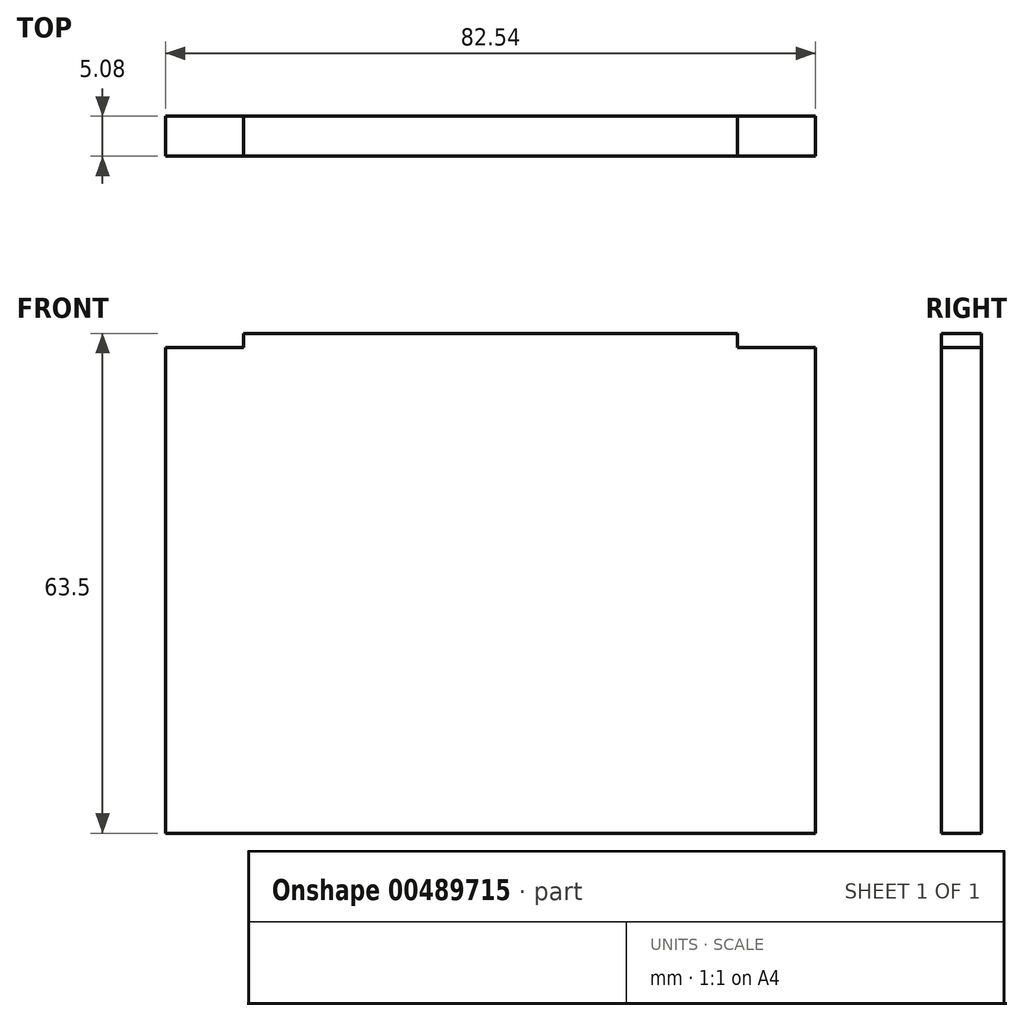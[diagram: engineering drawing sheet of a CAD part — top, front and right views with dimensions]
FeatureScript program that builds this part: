
annotation { "Feature Type Name" : "Feature", "Feature Type Description" : "" }
export const myFeature = defineFeature(function(context is Context, id is Id, definition is map)
    precondition{}
    {
        {
            var Q0;
            Q0=qCreatedBy(makeId("Front.planeOp"),FACE);
            var sketch = newSketch(context, id + "F0", { "sketchPlane" : qUnion([Q0])});
            skLineSegment(sketch, "E0.bottom", {"start": v(41.28, -31.75) * mm, "end": v(-41.28, -31.75) * mm});
            skLineSegment(sketch, "E0.top", {"start": v(31.37, 31.75) * mm, "end": v(-31.37, 31.75) * mm});
            skLineSegment(sketch, "E0.left", {"start": v(41.28, -31.75) * mm, "end": v(41.28, 29.97) * mm});
            skLineSegment(sketch, "E0.right", {"start": v(-41.28, -31.75) * mm, "end": v(-41.28, 29.97) * mm});
            skPoint(sketch, "E0.middle", {"position": v(0, 0) * mm});
            skLineSegment(sketch, "E1.top", {"start": v(-41.27, 29.97) * mm, "end": v(-31.37, 29.97) * mm});
            skLineSegment(sketch, "E1.right", {"start": v(-31.37, 31.75) * mm, "end": v(-31.37, 29.97) * mm});
            skLineSegment(sketch, "E2.MirrorCS", {"start": v(41.27, 29.97) * mm, "end": v(31.37, 29.97) * mm});
            skLineSegment(sketch, "E3.MirrorCS", {"start": v(31.37, 31.75) * mm, "end": v(31.37, 29.97) * mm});
            skPoint(sketch, "E4.orphan", {"position": v(41.28, 31.75) * mm});
            skPoint(sketch, "E5.orphan", {"position": v(-41.28, 31.75) * mm});
            skSolve(sketch);
        }
        {
            var Q0;
            Q0=makeQuery(id+"F0.imprint","IMPRINT",FACE,{"disambiguationData":[TD([[makeQuery(id+"F0.imprint","IMPRINT",EDGE,{"derivedFrom":sQuery(id+"F0.wireOp",EDGE,"E0.bottom")}),-1.0]])]});
            extrude(context, id + "F1", {"entities" : qUnion([Q0]), "depth" : 5.08 * mm});
        }
    });
